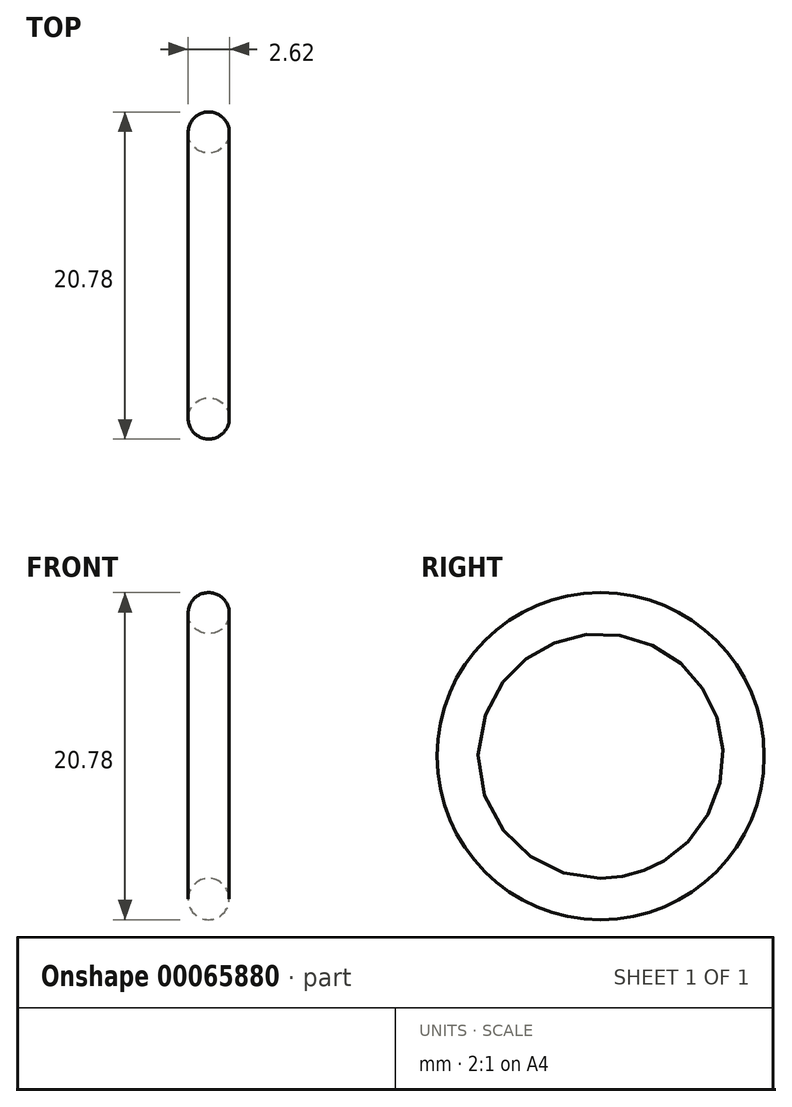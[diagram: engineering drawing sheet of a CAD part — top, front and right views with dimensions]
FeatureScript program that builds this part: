
annotation { "Feature Type Name" : "Feature", "Feature Type Description" : "" }
export const myFeature = defineFeature(function(context is Context, id is Id, definition is map)
    precondition{}
    {
        {
            var Q0;
            Q0=qCreatedBy(makeId("Front.planeOp"),FACE);
            var sketch = newSketch(context, id + "F0", { "sketchPlane" : qUnion([Q0])});
            skLineSegment(sketch, "E0", {"start": v(0, 0) * mm, "end": v(-6.06, 0) * mm, "construction": true});
            skCircle(sketch, "E1", {"center": v(0, 9.08) * mm, "radius": 1.3 * mm});
            skSolve(sketch);
        }
        {
            var Q0;
            Q0=makeQuery(id+"F0.imprint","IMPRINT",FACE,{"disambiguationData":[TD([[makeQuery(id+"F0.imprint","IMPRINT",EDGE,{"derivedFrom":sQuery(id+"F0.wireOp",EDGE,"E1")}),1.0]])]});
            var Q1;
            Q1=sQuery(id+"F0.wireOp",EDGE,"E0");
            revolve(context, id + "F1", {"entities" : qUnion([Q0]), "axis" : qUnion([Q1]), "revolveType" : RevolveType.FULL});
        }
    });
